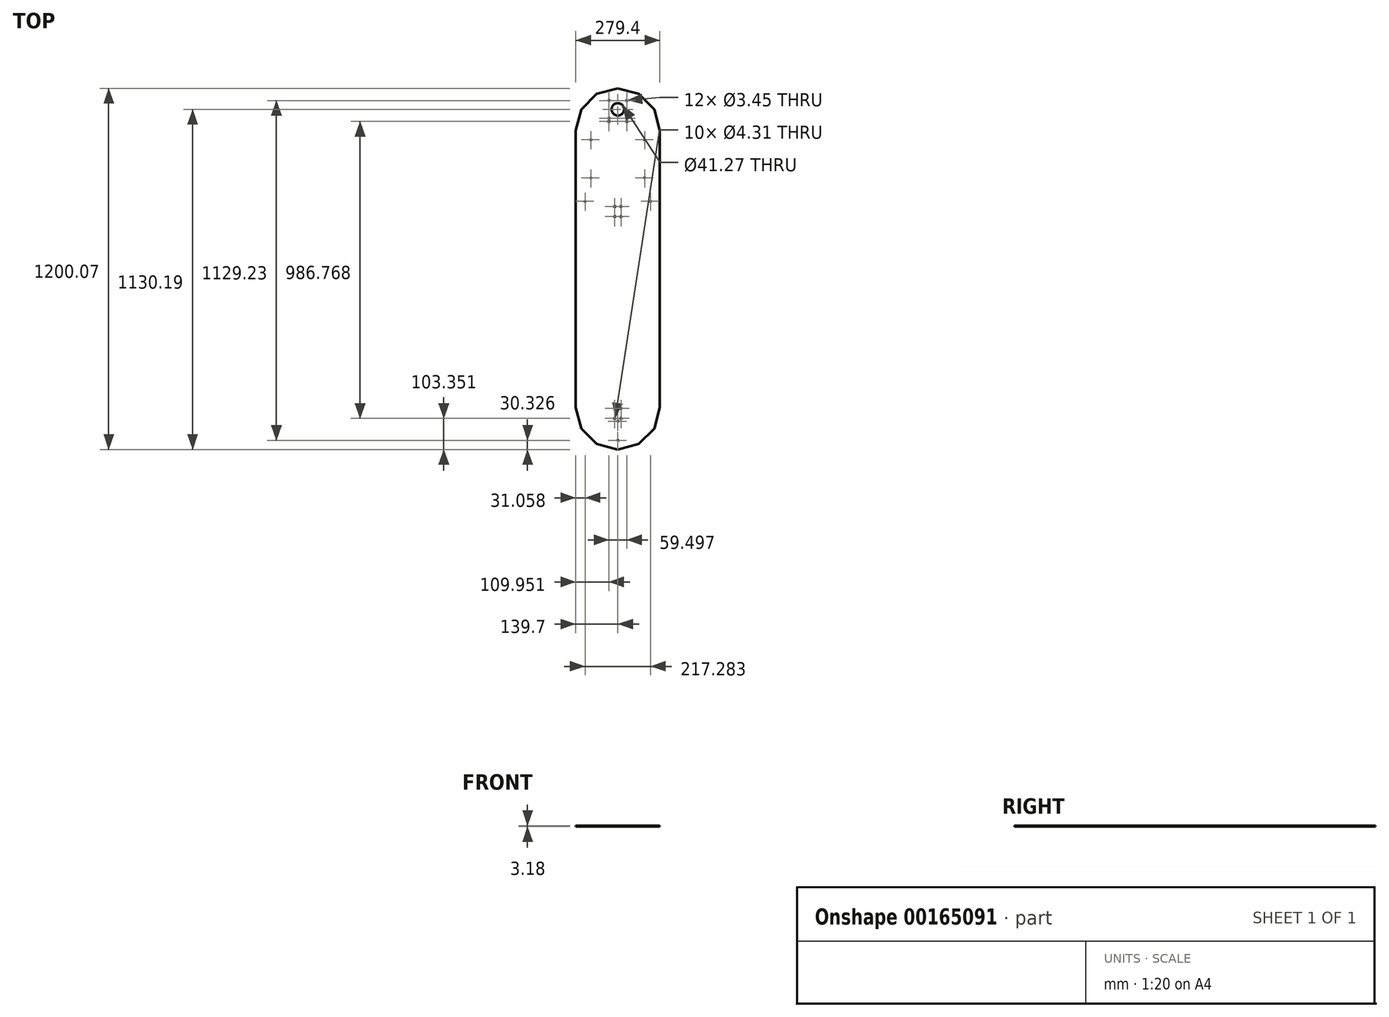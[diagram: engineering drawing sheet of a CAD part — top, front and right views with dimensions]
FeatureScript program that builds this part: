
annotation { "Feature Type Name" : "Feature", "Feature Type Description" : "" }
export const myFeature = defineFeature(function(context is Context, id is Id, definition is map)
    precondition{}
    {
        {
            var Q0;
            Q0=qCreatedBy(makeId("Top.planeOp"),FACE);
            var sketch = newSketch(context, id + "F0", { "sketchPlane" : qUnion([Q0])});
            skLineSegment(sketch, "E0", {"start": v(139.7, 0) * mm, "end": v(279.4, 0) * mm, "construction": true});
            skLineSegment(sketch, "E1", {"start": v(139.7, 0) * mm, "end": v(260.68, 69.85) * mm, "construction": true});
            skLineSegment(sketch, "E2", {"start": v(139.7, 0) * mm, "end": v(209.55, 120.98) * mm, "construction": true});
            skLineSegment(sketch, "E3", {"start": v(139.7, 0) * mm, "end": v(139.7, 139.7) * mm, "construction": true});
            skLineSegment(sketch, "E4", {"start": v(279.4, 0) * mm, "end": v(260.68, 69.85) * mm});
            skLineSegment(sketch, "E5", {"start": v(260.68, 69.85) * mm, "end": v(209.55, 120.98) * mm});
            skLineSegment(sketch, "E6", {"start": v(209.55, 120.98) * mm, "end": v(139.7, 139.7) * mm});
            skLineSegment(sketch, "E7", {"start": v(279.4, 0) * mm, "end": v(279.4, -920.67) * mm});
            skLineSegment(sketch, "E8", {"start": v(279.4, -920.67) * mm, "end": v(139.7, -920.67) * mm, "construction": true});
            skLineSegment(sketch, "E9", {"start": v(139.7, -920.67) * mm, "end": v(260.68, -990.52) * mm, "construction": true});
            skLineSegment(sketch, "E10", {"start": v(139.7, 0) * mm, "end": v(69.85, 120.98) * mm, "construction": true});
            skLineSegment(sketch, "E11", {"start": v(139.7, 0) * mm, "end": v(18.72, 69.85) * mm, "construction": true});
            skLineSegment(sketch, "E12", {"start": v(139.7, 0) * mm, "end": v(0, 0) * mm, "construction": true});
            skLineSegment(sketch, "E13", {"start": v(139.7, -920.67) * mm, "end": v(0, -920.67) * mm, "construction": true});
            skLineSegment(sketch, "E14", {"start": v(139.7, 139.7) * mm, "end": v(69.85, 120.98) * mm});
            skLineSegment(sketch, "E15", {"start": v(69.85, 120.98) * mm, "end": v(18.72, 69.85) * mm});
            skLineSegment(sketch, "E16", {"start": v(18.72, 69.85) * mm, "end": v(0, 0) * mm});
            skLineSegment(sketch, "E17", {"start": v(0, 0) * mm, "end": v(0, -920.67) * mm});
            skLineSegment(sketch, "E18", {"start": v(139.7, -920.67) * mm, "end": v(209.55, -1041.66) * mm, "construction": true});
            skLineSegment(sketch, "E19", {"start": v(139.7, -920.67) * mm, "end": v(139.7, -1060.37) * mm, "construction": true});
            skLineSegment(sketch, "E20", {"start": v(139.7, -920.67) * mm, "end": v(69.85, -1041.66) * mm, "construction": true});
            skLineSegment(sketch, "E21", {"start": v(139.7, -920.67) * mm, "end": v(18.72, -990.52) * mm, "construction": true});
            skLineSegment(sketch, "E22", {"start": v(0, -920.67) * mm, "end": v(18.72, -990.52) * mm});
            skLineSegment(sketch, "E23", {"start": v(18.72, -990.52) * mm, "end": v(69.85, -1041.66) * mm});
            skLineSegment(sketch, "E24", {"start": v(69.85, -1041.66) * mm, "end": v(139.7, -1060.37) * mm});
            skLineSegment(sketch, "E25", {"start": v(139.7, -1060.37) * mm, "end": v(209.55, -1041.66) * mm});
            skLineSegment(sketch, "E26", {"start": v(209.55, -1041.66) * mm, "end": v(260.68, -990.52) * mm});
            skLineSegment(sketch, "E27", {"start": v(260.68, -990.52) * mm, "end": v(279.4, -920.67) * mm});
            skSolve(sketch);
        }
        {
            var Q0;
            Q0=qSketchRegion(id+"F0",true);
            extrude(context, id + "F1", {"entities" : qUnion([Q0]), "depth" : 3.17 * mm});
        }
        {
            var Q0;
            Q0=makeQuery(id+"F1.opExtrude","CAP_FACE",FACE,{"disambiguationData":[OSD([sQuery(id+"F0.wireOp",EDGE,"E4"),sQuery(id+"F0.wireOp",EDGE,"E5"),sQuery(id+"F0.wireOp",EDGE,"E6"),sQuery(id+"F0.wireOp",EDGE,"E7"),sQuery(id+"F0.wireOp",EDGE,"E14"),sQuery(id+"F0.wireOp",EDGE,"E15"),sQuery(id+"F0.wireOp",EDGE,"E16"),sQuery(id+"F0.wireOp",EDGE,"E17"),sQuery(id+"F0.wireOp",EDGE,"E22"),sQuery(id+"F0.wireOp",EDGE,"E23"),sQuery(id+"F0.wireOp",EDGE,"E24"),sQuery(id+"F0.wireOp",EDGE,"E25"),sQuery(id+"F0.wireOp",EDGE,"E26"),sQuery(id+"F0.wireOp",EDGE,"E27")])],"isStart":false});
            var sketch = newSketch(context, id + "F2", { "sketchPlane" : qUnion([Q0])});
            skLineSegment(sketch, "E28", {"start": v(139.7, 139.7) * mm, "end": v(139.7, 113.4) * mm, "construction": true});
            skLineSegment(sketch, "E29", {"start": v(139.7, 113.4) * mm, "end": v(209.55, 94.69) * mm, "construction": true});
            skLineSegment(sketch, "E30", {"start": v(139.7, 113.4) * mm, "end": v(83, 98.21) * mm, "construction": true});
            skLineSegment(sketch, "E31", {"start": v(209.55, 120.98) * mm, "end": v(209.55, 94.69) * mm, "construction": true});
            skLineSegment(sketch, "E32", {"start": v(83, 98.21) * mm, "end": v(69.85, 120.98) * mm, "construction": true});
            skLineSegment(sketch, "E33.bottom", {"start": v(169.07, 99.18) * mm, "end": v(110.33, 99.18) * mm, "construction": true});
            skLineSegment(sketch, "E33.top", {"start": v(169.07, 40.45) * mm, "end": v(110.33, 40.45) * mm, "construction": true});
            skLineSegment(sketch, "E33.left", {"start": v(169.07, 99.18) * mm, "end": v(169.07, 40.45) * mm, "construction": true});
            skLineSegment(sketch, "E33.right", {"start": v(110.33, 99.18) * mm, "end": v(110.33, 40.45) * mm, "construction": true});
            skPoint(sketch, "E33.middle", {"position": v(139.7, 69.82) * mm});
            skCircle(sketch, "E34", {"center": v(139.7, 69.82) * mm, "radius": 20.64 * mm});
            skLineSegment(sketch, "E35", {"start": v(169.07, 99.18) * mm, "end": v(169.07, 105.53) * mm, "construction": true});
            skLineSegment(sketch, "E36", {"start": v(139.7, 69.82) * mm, "end": v(139.7, 113.4) * mm, "construction": true});
            skLineSegment(sketch, "E37", {"start": v(139.7, 69.82) * mm, "end": v(139.7, -94.44) * mm, "construction": true});
            skLineSegment(sketch, "E38", {"start": v(139.7, -94.44) * mm, "end": v(229.1, -31.14) * mm, "construction": true});
            skLineSegment(sketch, "E39", {"start": v(229.1, -94.44) * mm, "end": v(229.1, -157.74) * mm, "construction": true});
            skLineSegment(sketch, "E40", {"start": v(229.1, -157.74) * mm, "end": v(139.7, -94.44) * mm, "construction": true});
            skLineSegment(sketch, "E41", {"start": v(139.7, -94.44) * mm, "end": v(50.3, -31.14) * mm, "construction": true});
            skLineSegment(sketch, "E42", {"start": v(50.3, -157.74) * mm, "end": v(139.7, -94.44) * mm, "construction": true});
            skCircle(sketch, "E43", {"center": v(229.1, -31.14) * mm, "radius": 1.73 * mm});
            skCircle(sketch, "E44", {"center": v(229.1, -157.74) * mm, "radius": 1.73 * mm});
            skCircle(sketch, "E45", {"center": v(110.33, 40.45) * mm, "radius": 1.73 * mm});
            skCircle(sketch, "E46", {"center": v(169.07, 40.45) * mm, "radius": 1.73 * mm});
            skCircle(sketch, "E47", {"center": v(169.07, 99.18) * mm, "radius": 1.73 * mm});
            skCircle(sketch, "E48", {"center": v(110.33, 99.18) * mm, "radius": 1.73 * mm});
            skCircle(sketch, "E49", {"center": v(50.3, -157.74) * mm, "radius": 1.73 * mm});
            skCircle(sketch, "E50", {"center": v(50.3, -31.14) * mm, "radius": 1.73 * mm});
            skLineSegment(sketch, "E51", {"start": v(139.7, -94.44) * mm, "end": v(229.1, -94.44) * mm, "construction": true});
            skLineSegment(sketch, "E52", {"start": v(139.7, -94.44) * mm, "end": v(50.3, -94.44) * mm, "construction": true});
            skLineSegment(sketch, "E53", {"start": v(50.3, -94.44) * mm, "end": v(50.3, -157.74) * mm, "construction": true});
            skLineSegment(sketch, "E54", {"start": v(50.3, -94.44) * mm, "end": v(50.3, -31.14) * mm, "construction": true});
            skLineSegment(sketch, "E55", {"start": v(229.1, -94.44) * mm, "end": v(229.1, -31.14) * mm, "construction": true});
            skLineSegment(sketch, "E56", {"start": v(139.7, -94.44) * mm, "end": v(139.7, -235.73) * mm, "construction": true});
            skLineSegment(sketch, "E57", {"start": v(31.06, -235.73) * mm, "end": v(248.34, -235.73) * mm, "construction": true});
            skLineSegment(sketch, "E58", {"start": v(248.34, -235.73) * mm, "end": v(279.4, -235.73) * mm, "construction": true});
            skLineSegment(sketch, "E59", {"start": v(139.7, -235.73) * mm, "end": v(139.7, -253.19) * mm, "construction": true});
            skLineSegment(sketch, "E60.bottom", {"start": v(129.38, -253.19) * mm, "end": v(150.02, -253.19) * mm, "construction": true});
            skLineSegment(sketch, "E60.top", {"start": v(129.38, -286.53) * mm, "end": v(150.02, -286.53) * mm, "construction": true});
            skLineSegment(sketch, "E60.left", {"start": v(129.38, -253.19) * mm, "end": v(129.38, -286.53) * mm, "construction": true});
            skLineSegment(sketch, "E60.right", {"start": v(150.02, -253.19) * mm, "end": v(150.02, -286.53) * mm, "construction": true});
            skCircle(sketch, "E61", {"center": v(248.34, -235.73) * mm, "radius": 1.73 * mm});
            skCircle(sketch, "E62", {"center": v(31.06, -235.73) * mm, "radius": 1.73 * mm});
            skCircle(sketch, "E63", {"center": v(150.02, -286.53) * mm, "radius": 2.15 * mm});
            skCircle(sketch, "E64", {"center": v(129.38, -286.53) * mm, "radius": 2.15 * mm});
            skCircle(sketch, "E65", {"center": v(129.38, -253.19) * mm, "radius": 2.15 * mm});
            skCircle(sketch, "E66", {"center": v(150.02, -253.19) * mm, "radius": 2.15 * mm});
            skLineSegment(sketch, "E67", {"start": v(139.7, -253.19) * mm, "end": v(139.7, -269.86) * mm, "construction": true});
            skLineSegment(sketch, "E68", {"start": v(139.7, -269.86) * mm, "end": v(150.02, -269.86) * mm, "construction": true});
            skLineSegment(sketch, "E69", {"start": v(139.7, -269.86) * mm, "end": v(139.7, -940.35) * mm, "construction": true});
            skLineSegment(sketch, "E70.bottom", {"start": v(150.02, -923.68) * mm, "end": v(129.38, -923.68) * mm, "construction": true});
            skLineSegment(sketch, "E70.top", {"start": v(150.02, -957.02) * mm, "end": v(129.38, -957.02) * mm, "construction": true});
            skLineSegment(sketch, "E70.left", {"start": v(150.02, -923.68) * mm, "end": v(150.02, -957.02) * mm, "construction": true});
            skLineSegment(sketch, "E70.right", {"start": v(129.38, -923.68) * mm, "end": v(129.38, -957.02) * mm, "construction": true});
            skPoint(sketch, "E70.middle", {"position": v(139.7, -940.35) * mm});
            skCircle(sketch, "E71", {"center": v(129.38, -923.68) * mm, "radius": 2.15 * mm});
            skCircle(sketch, "E72", {"center": v(150.02, -923.68) * mm, "radius": 2.15 * mm});
            skCircle(sketch, "E73", {"center": v(150.02, -957.02) * mm, "radius": 2.15 * mm});
            skCircle(sketch, "E74", {"center": v(129.38, -957.02) * mm, "radius": 2.15 * mm});
            skLineSegment(sketch, "E75", {"start": v(139.7, -940.35) * mm, "end": v(139.7, -966.54) * mm, "construction": true});
            skLineSegment(sketch, "E76", {"start": v(139.7, -966.54) * mm, "end": v(139.7, -1030.04) * mm, "construction": true});
            skLineSegment(sketch, "E77", {"start": v(139.7, -1030.04) * mm, "end": v(139.7, -1060.37) * mm, "construction": true});
            skCircle(sketch, "E78", {"center": v(139.7, -966.54) * mm, "radius": 1.73 * mm});
            skCircle(sketch, "E79", {"center": v(139.7, -1030.04) * mm, "radius": 1.73 * mm});
            skSolve(sketch);
        }
        {
            var Q0;
            Q0 = qSketchRegion(id + "F2", true);
            var Q1;
            Q1=makeQuery(id+"F1.opExtrude","CAP_FACE",FACE,{"disambiguationData":[OSD([sQuery(id+"F0.wireOp",EDGE,"E4"),sQuery(id+"F0.wireOp",EDGE,"E5"),sQuery(id+"F0.wireOp",EDGE,"E6"),sQuery(id+"F0.wireOp",EDGE,"E7"),sQuery(id+"F0.wireOp",EDGE,"E14"),sQuery(id+"F0.wireOp",EDGE,"E15"),sQuery(id+"F0.wireOp",EDGE,"E16"),sQuery(id+"F0.wireOp",EDGE,"E17"),sQuery(id+"F0.wireOp",EDGE,"E22"),sQuery(id+"F0.wireOp",EDGE,"E23"),sQuery(id+"F0.wireOp",EDGE,"E24"),sQuery(id+"F0.wireOp",EDGE,"E25"),sQuery(id+"F0.wireOp",EDGE,"E26"),sQuery(id+"F0.wireOp",EDGE,"E27")])],"isStart":true});
            extrude(context, id + "F3", {"entities" : qUnion([Q0]), "operationType" : NewBodyOperationType.REMOVE, "endBound" : BoundingType.UP_TO_SURFACE, "oppositeDirection" : true, "endBoundEntityFace" : qUnion([Q1]), "depth" : 25.4 * mm});
        }
        {
            var Q0;
            Q0=makeQuery(id+"F1.opExtrude","CAP_FACE",FACE,{"disambiguationData":[OSD([sQuery(id+"F0.wireOp",EDGE,"E4"),sQuery(id+"F0.wireOp",EDGE,"E5"),sQuery(id+"F0.wireOp",EDGE,"E6"),sQuery(id+"F0.wireOp",EDGE,"E7"),sQuery(id+"F0.wireOp",EDGE,"E14"),sQuery(id+"F0.wireOp",EDGE,"E15"),sQuery(id+"F0.wireOp",EDGE,"E16"),sQuery(id+"F0.wireOp",EDGE,"E17"),sQuery(id+"F0.wireOp",EDGE,"E22"),sQuery(id+"F0.wireOp",EDGE,"E23"),sQuery(id+"F0.wireOp",EDGE,"E24"),sQuery(id+"F0.wireOp",EDGE,"E25"),sQuery(id+"F0.wireOp",EDGE,"E26"),sQuery(id+"F0.wireOp",EDGE,"E27")])],"isStart":false});
            var sketch = newSketch(context, id + "F4", { "sketchPlane" : qUnion([Q0])});
            skLineSegment(sketch, "E80", {"start": v(139.7, 139.7) * mm, "end": v(139.7, 29.75) * mm, "construction": true});
            skLineSegment(sketch, "E81", {"start": v(109.95, 29.75) * mm, "end": v(169.45, 29.75) * mm, "construction": true});
            skCircle(sketch, "E82", {"center": v(109.95, 29.75) * mm, "radius": 2.15 * mm});
            skCircle(sketch, "E83", {"center": v(169.45, 29.75) * mm, "radius": 2.15 * mm});
            skSolve(sketch);
        }
        {
            var Q0;
            Q0 = qSketchRegion(id + "F4", true);
            var Q1;
            Q1=makeQuery(id+"F1.opExtrude","CAP_FACE",FACE,{"disambiguationData":[OSD([sQuery(id+"F0.wireOp",EDGE,"E4"),sQuery(id+"F0.wireOp",EDGE,"E5"),sQuery(id+"F0.wireOp",EDGE,"E6"),sQuery(id+"F0.wireOp",EDGE,"E7"),sQuery(id+"F0.wireOp",EDGE,"E14"),sQuery(id+"F0.wireOp",EDGE,"E15"),sQuery(id+"F0.wireOp",EDGE,"E16"),sQuery(id+"F0.wireOp",EDGE,"E17"),sQuery(id+"F0.wireOp",EDGE,"E22"),sQuery(id+"F0.wireOp",EDGE,"E23"),sQuery(id+"F0.wireOp",EDGE,"E24"),sQuery(id+"F0.wireOp",EDGE,"E25"),sQuery(id+"F0.wireOp",EDGE,"E26"),sQuery(id+"F0.wireOp",EDGE,"E27")])],"isStart":true});
            extrude(context, id + "F5", {"entities" : qUnion([Q0]), "operationType" : NewBodyOperationType.REMOVE, "endBound" : BoundingType.UP_TO_SURFACE, "oppositeDirection" : true, "endBoundEntityFace" : qUnion([Q1]), "depth" : 25.4 * mm});
        }
    });
